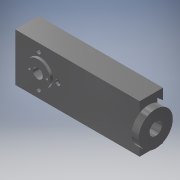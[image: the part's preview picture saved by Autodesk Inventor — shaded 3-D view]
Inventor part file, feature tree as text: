
AUTODESK INVENTOR PART (.ipt)
format: ipt  version: 2018 (Build 220112000, 112)  size: 229,888 bytes
history: native  units: mm
features: extrude x10, sketch x10
ambient origin geometry x8: Origin, YZ Plane, XZ Plane, XY Plane, X Axis, Y Axis, Z Axis, Center Point
bodies: Solid1 (feature_tree)
feature tree (20):
  extrude  "Extrusion1"  Depth=41.4mm
  extrude  "Extrusion2"  Depth=220.0mm
  extrude  "Extrusion3"  Depth=301.25mm TaperAngle=0.0deg
  extrude  "Extrusion4"  Depth=15.1mm
  extrude  "Extrusion5"  Depth=26.9mm TaperAngle=0.0deg
  extrude  "Extrusion6"  Depth=30.2mm
  extrude  "Extrusion7"  Depth=11.0mm
  extrude  "Extrusion8"  Depth=60.4mm
  extrude  "Extrusion9"  Depth=12.7mm
  extrude  "Extrusion10"  TaperAngle=90.0deg  [1 undecoded]
  sketch  "Sketch1"  dims[d0=85.0mm d1=41.4mm]
  sketch  "Sketch2"  dims[d2=220.0mm d3=0.0mm d4=19.0mm]
  sketch  "Sketch3"  dims[d8=19.0mm d9=301.25mm d10=0.0mm]
  sketch  "Sketch5"  dims[d12=15.1mm d13=15.1mm]
  sketch  "Sketch7"  dims[d14=141.9mm d15=26.9mm d16=0.0mm]
  sketch  "Sketch8"  dims[d17=28.6mm d18=30.2mm]
  sketch  "Sketch9"  dims[d19=4.6mm d21=11.0mm]
  sketch  "Sketch10"  dims[d22=91.9mm d23=0.0mm d24=60.4mm]
  sketch  "Sketch11"  dims[d25=12.7mm d26=0.0mm d27=10.6mm]
  sketch  "Sketch12"  dims[d28=83.6mm d29=90.0deg d30=4.9mm d31=6.0mm d32=0.0mm d33=22.0mm d34=22.3mm d35=22.7mm d36=22.15mm d37=0.0mm d38=4.6mm d39=0.0mm d40=17.5mm d41=310.85mm d42=0.0mm d43=4.4mm d44=5.0mm d45=4.4mm d46=2.5mm d47=3.5mm d48=0.0mm d49=40.7mm d50=9.4mm d51=4.0mm d52=40.7mm d53=9.4mm d54=4.0mm d55=70.6mm d56=39.5mm d57=4.5mm d58=4.5mm d59=7.0mm d60=0.0mm d61=8.726646mm d63=8.726646mm d64=10.0mm]
note: 1 required parameter value undecoded (feature->parameter linkage not recoverable at this tier; creation-order binding heuristic only, values carry confidence <= 0.55)
